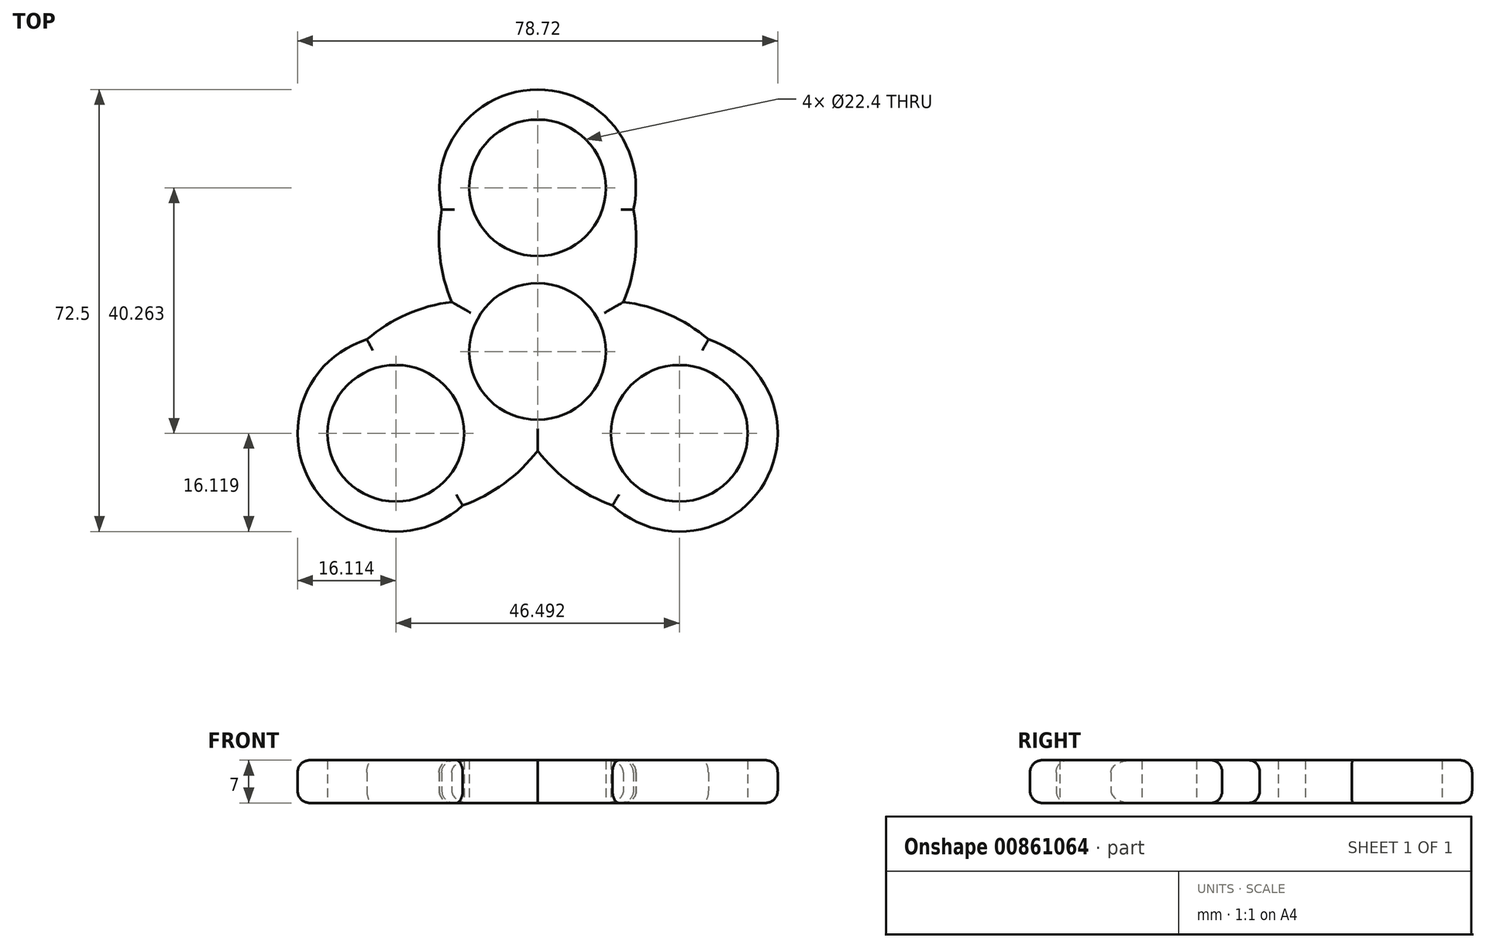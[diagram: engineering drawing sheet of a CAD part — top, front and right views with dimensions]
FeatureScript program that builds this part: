
annotation { "Feature Type Name" : "Feature", "Feature Type Description" : "" }
export const myFeature = defineFeature(function(context is Context, id is Id, definition is map)
    precondition{}
    {
        {
            var Q0;
            Q0=qCreatedBy(makeId("Top.planeOp"),FACE);
            var sketch = newSketch(context, id + "F0", { "sketchPlane" : qUnion([Q0])});
            skCircle(sketch, "E0", {"center": v(0, 0) * mm, "radius": 11.2 * mm});
            skCircle(sketch, "E1", {"center": v(0, 26.84) * mm, "radius": 11.2 * mm});
            skCircle(sketch, "E2.1.1", {"center": v(-23.25, -13.42) * mm, "radius": 11.2 * mm});
            skCircle(sketch, "E2.2.1", {"center": v(23.25, -13.42) * mm, "radius": 11.2 * mm});
            skArc(sketch, "E2.2.2", {"start": v(12.28, -25.23) * mm, "mid": v(37.2, -21.48) * mm, "end": v(28, 1.98) * mm});
            skArc(sketch, "E3", {"start": v(14.07, 8.13) * mm, "mid": v(16, 15.57) * mm, "end": v(15.7, 23.25) * mm});
            skArc(sketch, "E4.MirrorCS", {"start": v(14.07, 8.13) * mm, "mid": v(21.49, 6.08) * mm, "end": v(28, 1.98) * mm});
            skArc(sketch, "E5.1.0", {"start": v(-14.07, 8.13) * mm, "mid": v(-21.49, 6.08) * mm, "end": v(-28, 1.98) * mm});
            skArc(sketch, "E5.1.1", {"start": v(-14.07, 8.13) * mm, "mid": v(-16, 15.57) * mm, "end": v(-15.7, 23.25) * mm});
            skArc(sketch, "E5.2.0", {"start": v(0, -16.25) * mm, "mid": v(5.48, -21.65) * mm, "end": v(12.28, -25.23) * mm});
            skArc(sketch, "E5.2.1", {"start": v(0, -16.25) * mm, "mid": v(-5.48, -21.65) * mm, "end": v(-12.28, -25.23) * mm});
            skArc(sketch, "E6.1.0", {"start": v(15.7, 23.25) * mm, "mid": v(0, 42.96) * mm, "end": v(-15.7, 23.25) * mm});
            skArc(sketch, "E6.2.0", {"start": v(-28, 1.98) * mm, "mid": v(-37.2, -21.48) * mm, "end": v(-12.28, -25.23) * mm});
            skSolve(sketch);
        }
        {
            var Q0;
            Q0=makeQuery(id+"F0.imprint","IMPRINT",FACE,{"disambiguationData":[TD([[makeQuery(id+"F0.imprint","IMPRINT",EDGE,{"derivedFrom":sQuery(id+"F0.wireOp",EDGE,"E1")}),-1.0]])]});
            extrude(context, id + "F1", {"entities" : qUnion([Q0]), "depth" : 7 * mm, "offsetDistance" : 25 * mm});
        }
        {
            var Q0;
            Q0=makeQuery(id+"F1.opExtrude","CAP_EDGE",EDGE,{"disambiguationData":[OSD([sQuery(id+"F0.wireOp",EDGE,"E5.2.1")])],"isStart":false});
            var Q1;
            Q1=makeQuery(id+"F1.opExtrude","CAP_EDGE",EDGE,{"disambiguationData":[OSD([sQuery(id+"F0.wireOp",EDGE,"E2.1.2")])],"isStart":false});
            var Q2;
            Q2=makeQuery(id+"F1.opExtrude","CAP_EDGE",EDGE,{"disambiguationData":[OSD([sQuery(id+"F0.wireOp",EDGE,"E5.2.0")])],"isStart":false});
            var Q3;
            Q3=makeQuery(id+"F1.opExtrude","CAP_EDGE",EDGE,{"disambiguationData":[OSD([sQuery(id+"F0.wireOp",EDGE,"E2.2.2")])],"isStart":false});
            var Q4;
            Q4=makeQuery(id+"F1.opExtrude","CAP_EDGE",EDGE,{"disambiguationData":[OSD([sQuery(id+"F0.wireOp",EDGE,"E3")])],"isStart":false});
            var Q5;
            Q5=makeQuery(id+"F1.opExtrude","CAP_EDGE",EDGE,{"disambiguationData":[OSD([sQuery(id+"F0.wireOp",EDGE,"0On9TxZv-sKB3-iNfV-B8C3-GvCKJLezkO4Z")])],"isStart":false});
            var Q6;
            Q6=makeQuery(id+"F1.opExtrude","CAP_EDGE",EDGE,{"disambiguationData":[OSD([sQuery(id+"F0.wireOp",EDGE,"E5.1.1")])],"isStart":true});
            var Q7;
            Q7=makeQuery(id+"F1.opExtrude","CAP_EDGE",EDGE,{"disambiguationData":[OSD([sQuery(id+"F0.wireOp",EDGE,"E5.1.0")])],"isStart":true});
            var Q8;
            Q8=makeQuery(id+"F1.opExtrude","CAP_EDGE",EDGE,{"disambiguationData":[OSD([sQuery(id+"F0.wireOp",EDGE,"E2.1.2")])],"isStart":true});
            var Q9;
            Q9=makeQuery(id+"F1.opExtrude","CAP_EDGE",EDGE,{"disambiguationData":[OSD([sQuery(id+"F0.wireOp",EDGE,"E5.2.1")])],"isStart":true});
            var Q10;
            Q10=makeQuery(id+"F1.opExtrude","CAP_EDGE",EDGE,{"disambiguationData":[OSD([sQuery(id+"F0.wireOp",EDGE,"E5.2.0")])],"isStart":true});
            var Q11;
            Q11=makeQuery(id+"F1.opExtrude","CAP_EDGE",EDGE,{"disambiguationData":[OSD([sQuery(id+"F0.wireOp",EDGE,"E2.2.2")])],"isStart":true});
            var Q12;
            Q12=makeQuery(id+"F1.opExtrude","CAP_EDGE",EDGE,{"disambiguationData":[OSD([sQuery(id+"F0.wireOp",EDGE,"E3")])],"isStart":true});
            var Q13;
            Q13=makeQuery(id+"F1.opExtrude","CAP_EDGE",EDGE,{"disambiguationData":[OSD([sQuery(id+"F0.wireOp",EDGE,"0On9TxZv-sKB3-iNfV-B8C3-GvCKJLezkO4Z")])],"isStart":true});
            fillet(context, id + "F2", {"entities" : qUnion([Q0, Q1, Q2, Q3, Q4, Q5, Q6, Q7, Q8, Q9, Q10, Q11, Q12, Q13]), "radius" : 2 * mm, "tangentPropagation" : true, "allowEdgeOverflow" : false});
        }
        {
            var Q0;
            Q0=makeQuery(id+"F1.opExtrude","CAP_EDGE",EDGE,{"disambiguationData":[OSD([sQuery(id+"F0.wireOp",EDGE,"E6.1.0")])],"isStart":true});
            var Q1;
            Q1=makeQuery(id+"F1.opExtrude","CAP_EDGE",EDGE,{"disambiguationData":[OSD([sQuery(id+"F0.wireOp",EDGE,"E4.MirrorCS")])],"isStart":true});
            var Q2;
            Q2=makeQuery(id+"F1.opExtrude","CAP_EDGE",EDGE,{"disambiguationData":[OSD([sQuery(id+"F0.wireOp",EDGE,"E6.2.0")])],"isStart":true});
            var Q3;
            Q3=makeQuery(id+"F1.opExtrude","CAP_EDGE",EDGE,{"disambiguationData":[OSD([sQuery(id+"F0.wireOp",EDGE,"E4.MirrorCS")])],"isStart":false});
            var Q4;
            Q4=makeQuery(id+"F1.opExtrude","CAP_EDGE",EDGE,{"disambiguationData":[OSD([sQuery(id+"F0.wireOp",EDGE,"E6.1.0")])],"isStart":false});
            var Q5;
            Q5=makeQuery(id+"F1.opExtrude","CAP_EDGE",EDGE,{"disambiguationData":[OSD([sQuery(id+"F0.wireOp",EDGE,"E5.1.1")])],"isStart":false});
            var Q6;
            Q6=makeQuery(id+"F1.opExtrude","CAP_EDGE",EDGE,{"disambiguationData":[OSD([sQuery(id+"F0.wireOp",EDGE,"E5.1.0")])],"isStart":false});
            var Q7;
            Q7=makeQuery(id+"F1.opExtrude","CAP_EDGE",EDGE,{"disambiguationData":[OSD([sQuery(id+"F0.wireOp",EDGE,"E6.2.0")])],"isStart":false});
            fillet(context, id + "F3", {"entities" : qUnion([Q0, Q1, Q2, Q3, Q4, Q5, Q6, Q7]), "radius" : 2 * mm, "tangentPropagation" : true, "allowEdgeOverflow" : false});
        }
    });
